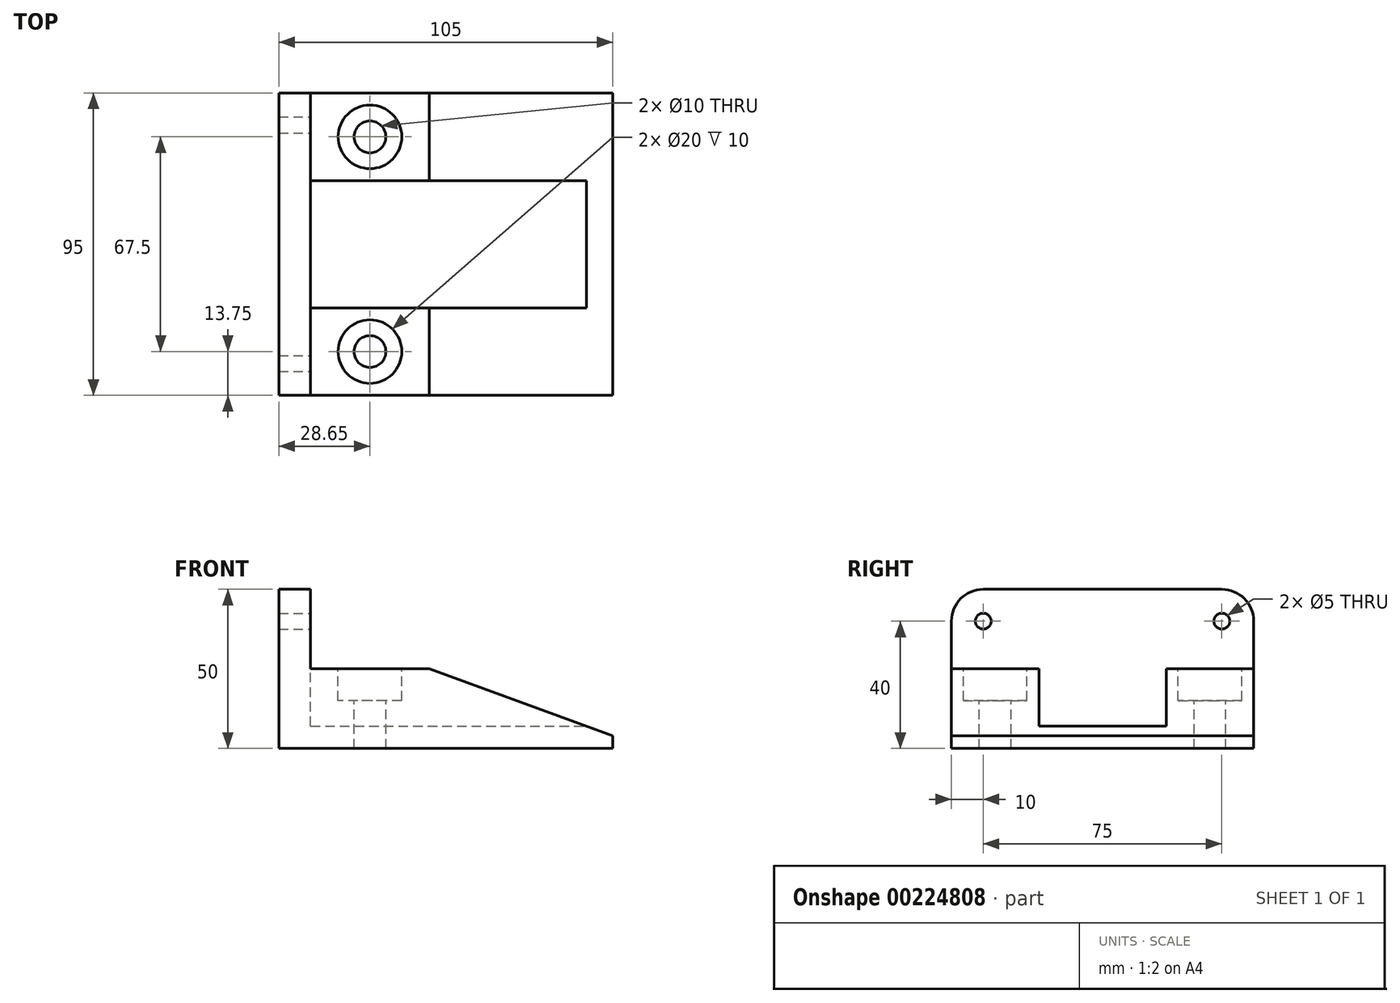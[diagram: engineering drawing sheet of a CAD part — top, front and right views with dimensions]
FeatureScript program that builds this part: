
annotation { "Feature Type Name" : "Feature", "Feature Type Description" : "" }
export const myFeature = defineFeature(function(context is Context, id is Id, definition is map)
    precondition{}
    {
        {
            var Q0;
            Q0=qCreatedBy(makeId("Top.planeOp"),FACE);
            var sketch = newSketch(context, id + "F0", { "sketchPlane" : qUnion([Q0])});
            skLineSegment(sketch, "E0.bottom", {"start": v(52.5, -47.5) * mm, "end": v(-52.5, -47.5) * mm});
            skLineSegment(sketch, "E0.top", {"start": v(52.5, 47.5) * mm, "end": v(-52.5, 47.5) * mm});
            skLineSegment(sketch, "E0.left", {"start": v(52.5, -47.5) * mm, "end": v(52.5, 47.5) * mm});
            skLineSegment(sketch, "E0.right", {"start": v(-52.5, -47.5) * mm, "end": v(-52.5, 47.5) * mm});
            skPoint(sketch, "E0.middle", {"position": v(0, 0) * mm});
            skSolve(sketch);
        }
        {
            var Q0;
            Q0 = qSketchRegion(id + "F0", true);
            extrude(context, id + "F1", {"entities" : qUnion([Q0]), "depth" : 50 * mm});
        }
        {
            var Q0;
            Q0=makeQuery(id+"F1.opExtrude","CAP_FACE",FACE,{"disambiguationData":[OSD([sQuery(id+"F0.wireOp",EDGE,"E0.bottom"),sQuery(id+"F0.wireOp",EDGE,"E0.top"),sQuery(id+"F0.wireOp",EDGE,"E0.left"),sQuery(id+"F0.wireOp",EDGE,"E0.right")])],"isStart":false});
            var sketch = newSketch(context, id + "F2", { "sketchPlane" : qUnion([Q0])});
            skLineSegment(sketch, "E1", {"start": v(-42.5, 47.5) * mm, "end": v(-42.5, -47.5) * mm});
            skSolve(sketch);
        }
        {
            var Q0;
            {var subQ0=sQuery(id+"F2.wireOp",EDGE,"E1");Q0=makeQuery(id+"F2.imprint","IMPRINT",FACE,{"disambiguationData":[TD([[makeQuery(id+"F2.imprint","IMPRINT",EDGE,{"derivedFrom":subQ0}),1.0]])]});}
            extrude(context, id + "F3", {"entities" : qUnion([Q0]), "operationType" : NewBodyOperationType.REMOVE, "oppositeDirection" : true, "depth" : 25 * mm});
        }
        {
            var Q0;
            Q0=makeQuery(id+"F3.boolean.opBoolean","COPY",FACE,{"derivedFrom":makeQuery(id+"F3.opExtrude","CAP_FACE",FACE,{"disambiguationData":[OSD([sQuery(id+"F0.wireOp",EDGE,"E0.bottom"),sQuery(id+"F0.wireOp",EDGE,"E0.top"),sQuery(id+"F0.wireOp",EDGE,"E0.left"),sQuery(id+"F2.wireOp",EDGE,"E1")])],"isStart":false})});
            var sketch = newSketch(context, id + "F4", { "sketchPlane" : qUnion([Q0])});
            skLineSegment(sketch, "E2", {"start": v(-5.2, 47.5) * mm, "end": v(-5.2, -47.5) * mm});
            skLineSegment(sketch, "E3.bottom", {"start": v(-42.5, 20) * mm, "end": v(52.5, 20) * mm});
            skLineSegment(sketch, "E3.top", {"start": v(-42.5, -20) * mm, "end": v(52.5, -20) * mm});
            skLineSegment(sketch, "E3.left", {"start": v(-42.5, 20) * mm, "end": v(-42.5, -20) * mm});
            skLineSegment(sketch, "E3.right", {"start": v(52.5, 20) * mm, "end": v(52.5, -20) * mm});
            skSolve(sketch);
        }
        {
            var Q0;
            Q0=makeQuery(id+"F1.opExtrude","SWEPT_FACE",FACE,{"disambiguationData":[OSD([sQuery(id+"F0.wireOp",EDGE,"E0.bottom")])]});
            var sketch = newSketch(context, id + "F5", { "sketchPlane" : qUnion([Q0])});
            skPoint(sketch, "E4.0", {"position": v(-5.2, 25) * mm});
            skLineSegment(sketch, "E5", {"start": v(-5.2, 25) * mm, "end": v(52.5, 4) * mm});
            skLineSegment(sketch, "E6", {"start": v(-5.2, 25) * mm, "end": v(52.5, 25) * mm});
            skLineSegment(sketch, "E7", {"start": v(52.5, 25) * mm, "end": v(52.5, 4) * mm});
            skSolve(sketch);
        }
        {
            var Q0;
            Q0=makeQuery(id+"F5.imprint","IMPRINT",FACE,{"disambiguationData":[TD([[makeQuery(id+"F5.imprint","IMPRINT",EDGE,{"derivedFrom":sQuery(id+"F5.wireOp",EDGE,"E5")}),1.0]])]});
            extrude(context, id + "F6", {"entities" : qUnion([Q0]), "operationType" : NewBodyOperationType.REMOVE, "endBound" : BoundingType.THROUGH_ALL, "oppositeDirection" : true, "depth" : 25 * mm});
        }
        {
            var Q0;
            Q0 = qSketchRegion(id + "F4", true);
            extrude(context, id + "F7", {"entities" : qUnion([Q0]), "operationType" : NewBodyOperationType.REMOVE, "oppositeDirection" : true, "depth" : 18 * mm});
        }
        {
            var Q0;
            Q0=makeQuery(id+"F1.opExtrude","CAP_EDGE",EDGE,{"disambiguationData":[OSD([sQuery(id+"F0.wireOp",EDGE,"E0.bottom")])],"isStart":false});
            var Q1;
            Q1=makeQuery(id+"F1.opExtrude","CAP_EDGE",EDGE,{"disambiguationData":[OSD([sQuery(id+"F0.wireOp",EDGE,"E0.top")])],"isStart":false});
            fillet(context, id + "F8", {"entities" : qUnion([Q0, Q1]), "radius" : 10 * mm, "tangentPropagation" : true, "allowEdgeOverflow" : false});
        }
        {
            var Q0;
            Q0=makeQuery(id+"F7.boolean.opBoolean","MERGE",FACE,{"derivedFrom":[makeQuery(id+"F3.boolean.opBoolean","COPY",FACE,{"derivedFrom":makeQuery(id+"F3.opExtrude","SWEPT_FACE",FACE,{"disambiguationData":[OSD([sQuery(id+"F2.wireOp",EDGE,"E1")])]})}),makeQuery(id+"F7.opExtrude","SWEPT_FACE",FACE,{"disambiguationData":[OSD([sQuery(id+"F4.wireOp",EDGE,"E3.left")])]})]});
            var sketch = newSketch(context, id + "F9", { "sketchPlane" : qUnion([Q0])});
            skLineSegment(sketch, "E8", {"start": v(-37.5, 50) * mm, "end": v(-37.5, 40) * mm});
            skLineSegment(sketch, "E9", {"start": v(-37.5, 40) * mm, "end": v(-47.5, 40) * mm});
            skCircle(sketch, "E10", {"center": v(-37.5, 40) * mm, "radius": 2.5 * mm});
            skCircle(sketch, "E11.MirrorC", {"center": v(37.5, 40) * mm, "radius": 2.5 * mm});
            skSolve(sketch);
        }
        {
            var Q0;
            Q0 = qSketchRegion(id + "F9", true);
            extrude(context, id + "F10", {"entities" : qUnion([Q0]), "operationType" : NewBodyOperationType.REMOVE, "endBound" : BoundingType.THROUGH_ALL, "oppositeDirection" : true, "depth" : 25 * mm});
        }
        {
            var Q0;
            {var subQ0=sQuery(id+"F0.wireOp",EDGE,"E0.bottom");var subQ1=sQuery(id+"F2.wireOp",EDGE,"E1");Q0=makeQuery(id+"F7.boolean.opBoolean","SPLIT",FACE,{"disambiguationData":[TD([makeQuery(id+"F1.opExtrude","SWEPT_FACE",FACE,{"disambiguationData":[OSD([subQ0])]})])],"derivedFrom":makeQuery(id+"F3.boolean.opBoolean","COPY",FACE,{"derivedFrom":makeQuery(id+"F3.opExtrude","CAP_FACE",FACE,{"disambiguationData":[OSD([subQ0,sQuery(id+"F0.wireOp",EDGE,"E0.top"),sQuery(id+"F0.wireOp",EDGE,"E0.left"),subQ1])],"isStart":false})})});}
            var sketch = newSketch(context, id + "F11", { "sketchPlane" : qUnion([Q0])});
            skPoint(sketch, "E12", {"position": v(-23.85, -33.75) * mm});
            skPoint(sketch, "E12.positionSnap0", {"position": v(-5.2, -33.75) * mm});
            skPoint(sketch, "E12.positionSnap1", {"position": v(-23.85, -20) * mm});
            skLineSegment(sketch, "E13.0.0", {"start": v(-42.5, 47.5) * mm, "end": v(-42.5, 20) * mm});
            skLineSegment(sketch, "E13.0.1", {"start": v(-42.5, 20) * mm, "end": v(-5.2, 20) * mm});
            skLineSegment(sketch, "E13.0.2", {"start": v(-5.2, 20) * mm, "end": v(-5.2, 47.5) * mm});
            skLineSegment(sketch, "E13.0.3", {"start": v(-5.2, 47.5) * mm, "end": v(-42.5, 47.5) * mm});
            skPoint(sketch, "E14", {"position": v(-23.85, 33.75) * mm});
            skPoint(sketch, "E14.positionSnap0", {"position": v(-23.85, 47.5) * mm});
            skPoint(sketch, "E14.positionSnap1", {"position": v(-5.2, 33.75) * mm});
            skSolve(sketch);
        }
        {
            var Q0;
            Q0=sQuery(id+"F11.wireOp",VERTEX,"E14");
            var Q1;
            Q1=sQuery(id+"F11.wireOp",VERTEX,"E12");
            var Q2;
            Q2=makeQuery(id+"F1.opExtrude","SWEPT_BODY",BODY,{"disambiguationData":[OSD([sQuery(id+"F0.wireOp",EDGE,"E0.bottom"),sQuery(id+"F0.wireOp",EDGE,"E0.top"),sQuery(id+"F0.wireOp",EDGE,"E0.left"),sQuery(id+"F0.wireOp",EDGE,"E0.right")])]});
            hole(context, id + "F12", {"style" : HoleStyle.C_BORE, "endStyle" : HoleEndStyle.THROUGH, "holeDiameter" : 10 * mm, "cBoreDiameter" : 20 * mm, "cBoreDepth" : 10 * mm, "locations" : qUnion([Q0, Q1]), "scope" : qUnion([Q2]), "isTappedThrough" : true});
        }
    });
